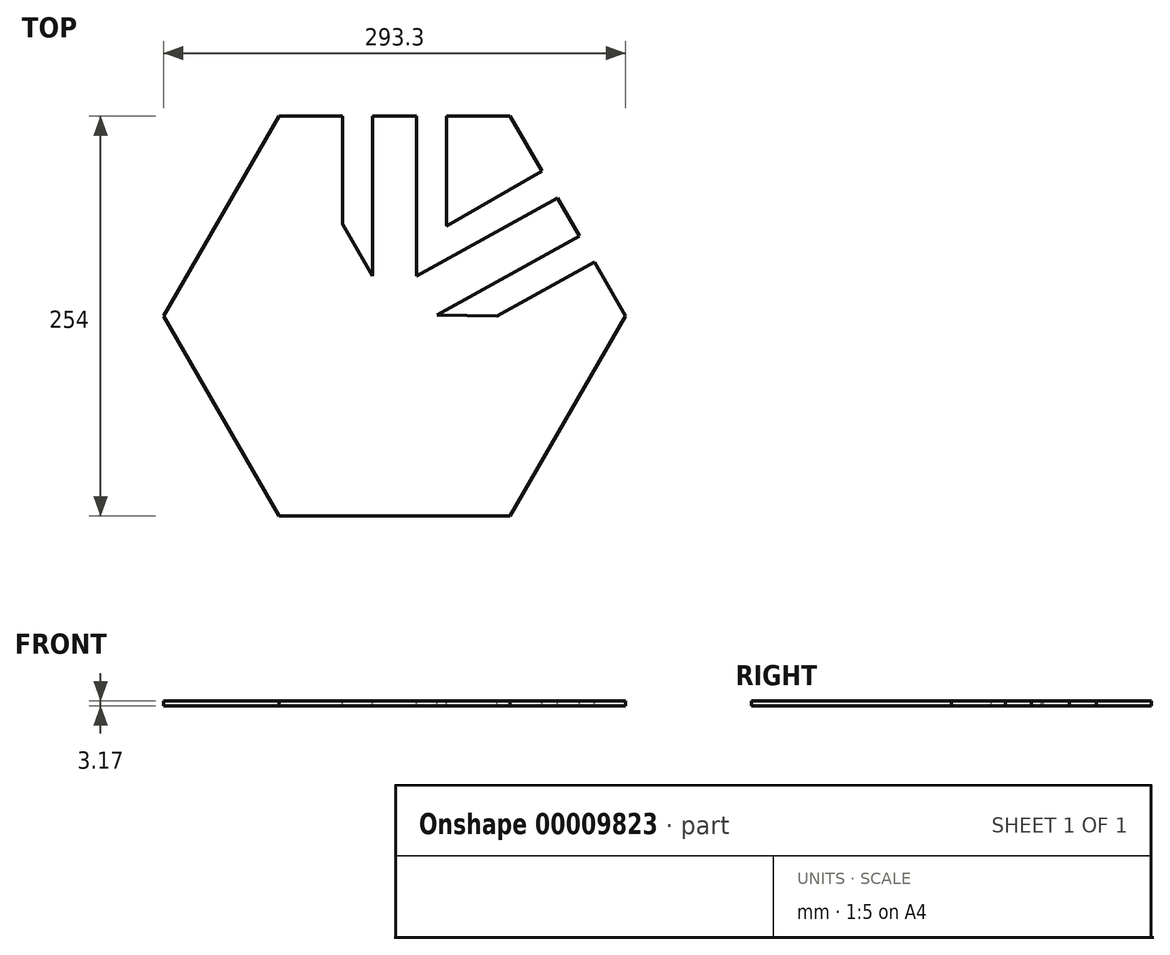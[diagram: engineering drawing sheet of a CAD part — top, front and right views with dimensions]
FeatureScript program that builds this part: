
annotation { "Feature Type Name" : "Feature", "Feature Type Description" : "" }
export const myFeature = defineFeature(function(context is Context, id is Id, definition is map)
    precondition{}
    {
        {
            var Q0;
            Q0=qCreatedBy(makeId("Top.planeOp"),FACE);
            var sketch = newSketch(context, id + "F0", { "sketchPlane" : qUnion([Q0])});
            skCircle(sketch, "E0.cCircle", {"center": v(0, 0) * mm, "radius": 127 * mm, "construction": true});
            skLineSegment(sketch, "E0.0", {"start": v(-73.32, 127) * mm, "end": v(73.32, 127) * mm});
            skLineSegment(sketch, "E0.1", {"start": v(73.32, 127) * mm, "end": v(146.65, 0) * mm});
            skLineSegment(sketch, "E0.2", {"start": v(146.65, 0) * mm, "end": v(73.32, -127) * mm});
            skLineSegment(sketch, "E0.3", {"start": v(73.32, -127) * mm, "end": v(-73.32, -127) * mm});
            skLineSegment(sketch, "E0.4", {"start": v(-73.32, -127) * mm, "end": v(-146.65, 0) * mm});
            skLineSegment(sketch, "E0.5", {"start": v(-146.65, 0) * mm, "end": v(-73.32, 127) * mm});
            skPoint(sketch, "E0.0.midPoint", {"position": v(0, 127) * mm});
            skSolve(sketch);
        }
        {
            var Q0;
            Q0=makeQuery(id+"F0.imprint","IMPRINT",FACE,{"disambiguationData":[TD([[makeQuery(id+"F0.imprint","IMPRINT",EDGE,{"derivedFrom":sQuery(id+"F0.wireOp",EDGE,"E0.0")}),-1.0]])]});
            extrude(context, id + "F1", {"entities" : qUnion([Q0]), "depth" : 3.17 * mm});
        }
        {
            var Q0;
            Q0=makeQuery(id+"F1.opExtrude","CAP_FACE",FACE,{"disambiguationData":[OSD([sQuery(id+"F0.wireOp",EDGE,"E0.0"),sQuery(id+"F0.wireOp",EDGE,"E0.1"),sQuery(id+"F0.wireOp",EDGE,"E0.2"),sQuery(id+"F0.wireOp",EDGE,"E0.3"),sQuery(id+"F0.wireOp",EDGE,"E0.4"),sQuery(id+"F0.wireOp",EDGE,"E0.5")])],"isStart":false});
            var sketch = newSketch(context, id + "F2", { "sketchPlane" : qUnion([Q0])});
            skLineSegment(sketch, "E1", {"start": v(13.97, 127) * mm, "end": v(13.97, 25.4) * mm});
            skLineSegment(sketch, "E2", {"start": v(13.97, 25.4) * mm, "end": v(33.02, 57.07) * mm});
            skLineSegment(sketch, "E3", {"start": v(33.02, 57.07) * mm, "end": v(33.02, 127) * mm});
            skLineSegment(sketch, "E4", {"start": v(13.97, 127) * mm, "end": v(33.02, 127) * mm});
            skLineSegment(sketch, "E5", {"start": v(-13.97, 127) * mm, "end": v(-13.97, 25.4) * mm});
            skLineSegment(sketch, "E6", {"start": v(-13.97, 25.4) * mm, "end": v(-33.02, 58.4) * mm});
            skLineSegment(sketch, "E7", {"start": v(-33.02, 58.4) * mm, "end": v(-33.02, 127) * mm});
            skLineSegment(sketch, "E8", {"start": v(-33.02, 127) * mm, "end": v(-13.97, 127) * mm});
            skLineSegment(sketch, "E9", {"start": v(13.97, 25.4) * mm, "end": v(103.4, 74.91) * mm});
            skLineSegment(sketch, "E10", {"start": v(103.4, 74.91) * mm, "end": v(93.53, 92) * mm});
            skLineSegment(sketch, "E11", {"start": v(93.53, 92) * mm, "end": v(33.02, 57.07) * mm});
            skLineSegment(sketch, "E12", {"start": v(117.37, 50.72) * mm, "end": v(27, 0.68) * mm});
            skLineSegment(sketch, "E13", {"start": v(27, 0.68) * mm, "end": v(65.1, 0) * mm});
            skLineSegment(sketch, "E14", {"start": v(65.1, 0) * mm, "end": v(126.9, 34.22) * mm});
            skLineSegment(sketch, "E15", {"start": v(126.9, 34.22) * mm, "end": v(117.37, 50.72) * mm});
            skPoint(sketch, "E16", {"position": v(0, 18.66) * mm});
            skSolve(sketch);
        }
        {
            var Q0;
            Q0=makeQuery(id+"F2.imprint","IMPRINT",FACE,{"disambiguationData":[TD([[makeQuery(id+"F2.imprint","IMPRINT",EDGE,{"derivedFrom":sQuery(id+"F2.wireOp",EDGE,"E5")}),-1.0]])]});
            var Q1;
            Q1=makeQuery(id+"F2.imprint","IMPRINT",FACE,{"disambiguationData":[TD([[makeQuery(id+"F2.imprint","IMPRINT",EDGE,{"derivedFrom":sQuery(id+"F2.wireOp",EDGE,"E1")}),1.0]])]});
            var Q2;
            Q2=makeQuery(id+"F2.imprint","IMPRINT",FACE,{"disambiguationData":[TD([[makeQuery(id+"F2.imprint","IMPRINT",EDGE,{"derivedFrom":sQuery(id+"F2.wireOp",EDGE,"E2")}),-1.0]])]});
            var Q3;
            Q3=makeQuery(id+"F2.imprint","IMPRINT",FACE,{"disambiguationData":[TD([[makeQuery(id+"F2.imprint","IMPRINT",EDGE,{"derivedFrom":sQuery(id+"F2.wireOp",EDGE,"E12")}),1.0]])]});
            var Q4;
            Q4=makeQuery(id+"F1.opExtrude","CAP_FACE",FACE,{"disambiguationData":[OSD([sQuery(id+"F0.wireOp",EDGE,"E0.0"),sQuery(id+"F0.wireOp",EDGE,"E0.1"),sQuery(id+"F0.wireOp",EDGE,"E0.2"),sQuery(id+"F0.wireOp",EDGE,"E0.3"),sQuery(id+"F0.wireOp",EDGE,"E0.4"),sQuery(id+"F0.wireOp",EDGE,"E0.5")])],"isStart":true});
            extrude(context, id + "F3", {"entities" : qUnion([Q0, Q1, Q2, Q3]), "operationType" : NewBodyOperationType.REMOVE, "endBound" : BoundingType.UP_TO_SURFACE, "oppositeDirection" : true, "endBoundEntityFace" : qUnion([Q4]), "depth" : 25.4 * mm});
        }
    });
